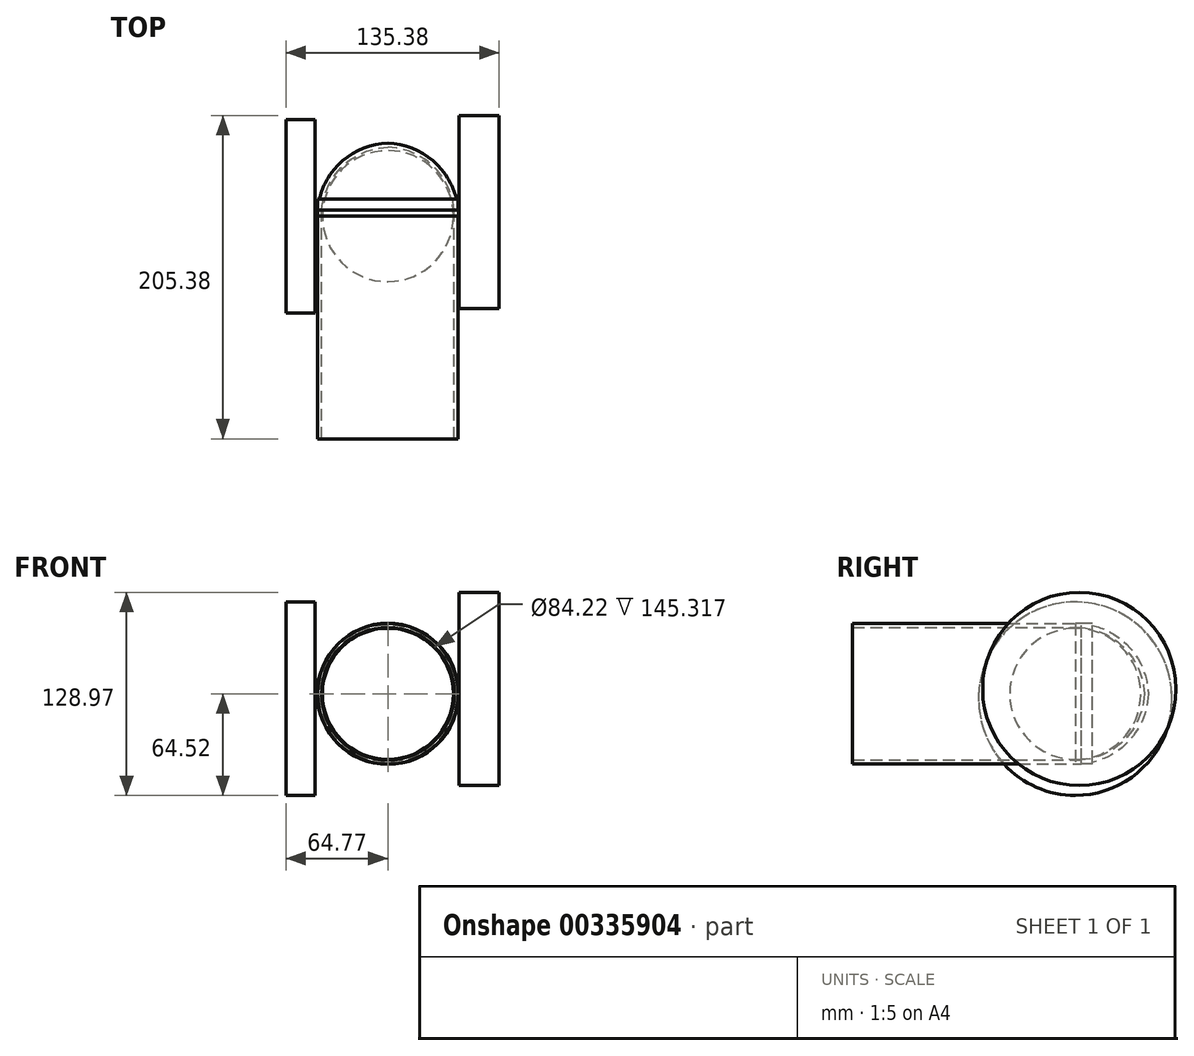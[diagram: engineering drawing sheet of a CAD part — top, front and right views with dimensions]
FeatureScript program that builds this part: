
annotation { "Feature Type Name" : "Feature", "Feature Type Description" : "" }
export const myFeature = defineFeature(function(context is Context, id is Id, definition is map)
    precondition{}
    {
        {
            var Q0;
            Q0=qCreatedBy(makeId("Front.planeOp"),FACE);
            var sketch = newSketch(context, id + "F0", { "sketchPlane" : qUnion([Q0])});
            skCircle(sketch, "E0", {"center": v(0, 0) * mm, "radius": 44.65 * mm});
            skSolve(sketch);
        }
        {
            var Q0;
            Q0 = qSketchRegion(id + "F0", true);
            extrude(context, id + "F1", {"entities" : qUnion([Q0]), "depth" : 76.2 * mm});
        }
        {
            var Q0;
            Q0=makeQuery(id+"F1.opExtrude","CAP_FACE",FACE,{"disambiguationData":[OSD([sQuery(id+"F0.wireOp",EDGE,"E0")])],"isStart":false});
            var sketch = newSketch(context, id + "F2", { "sketchPlane" : qUnion([Q0])});
            skSolve(sketch);
        }
        {
            var Q0;
            Q0=makeQuery(id+"F2.imprint","IMPRINT",FACE,{"disambiguationData":[TD([[makeQuery(id+"F2.imprint","IMPRINT",EDGE,{"derivedFrom":makeQuery(id+"F1.opExtrude","CAP_EDGE",EDGE,{"disambiguationData":[OSD([sQuery(id+"F0.wireOp",EDGE,"E0")])],"isStart":false})}),1.0]])]});
            extrude(context, id + "F3", {"entities" : qUnion([Q0]), "operationType" : NewBodyOperationType.ADD, "depth" : 25.4 * mm});
        }
        {
            var Q0;
            Q0=makeQuery(id+"F3.opExtrude","CAP_FACE",FACE,{"disambiguationData":[OSD([sQuery(id+"F0.wireOp",EDGE,"E0")])],"isStart":false});
            shell(context, id + "F4", {"entities" : qUnion([Q0]), "thickness" : 2.54 * mm});
        }
        {
            var Q0;
            Q0=qCreatedBy(makeId("Top.planeOp"),FACE);
            var sketch = newSketch(context, id + "F5", { "sketchPlane" : qUnion([Q0])});
            skArc(sketch, "E1", {"start": v(44.82, 0) * mm, "mid": v(31.78, 32.24) * mm, "end": v(0, 46.34) * mm});
            skLineSegment(sketch, "E2", {"start": v(0, 0) * mm, "end": v(44.82, 0) * mm});
            skLineSegment(sketch, "E3", {"start": v(0, 46.34) * mm, "end": v(0, 0) * mm});
            skSolve(sketch);
        }
        {
            var Q0;
            Q0=makeQuery(id+"F5.imprint","IMPRINT",FACE,{"disambiguationData":[TD([[makeQuery(id+"F5.imprint","IMPRINT",EDGE,{"derivedFrom":sQuery(id+"F5.wireOp",EDGE,"E1")}),1.0]])]});
            var Q1;
            Q1=sQuery(id+"F5.wireOp",EDGE,"E3");
            revolve(context, id + "F6", {"operationType" : NewBodyOperationType.ADD, "entities" : qUnion([Q0]), "axis" : qUnion([Q1]), "revolveType" : RevolveType.FULL});
        }
        {
            var Q0;
            {var subQ0=sQuery(id+"F0.wireOp",EDGE,"E0");Q0=makeQuery(id+"F4.opShell","OFFSET_FACE",FACE,{"disambiguationData":[OSD([subQ0]),TDD([makeQuery(id+"F1.opExtrude","CAP_FACE",FACE,{"disambiguationData":[OSD([subQ0])],"isStart":true})])]});}
            var sketch = newSketch(context, id + "F7", { "sketchPlane" : qUnion([Q0])});
            skCircle(sketch, "E4", {"center": v(0, 0) * mm, "radius": 42.16 * mm});
            skSolve(sketch);
        }
        {
            var Q0;
            Q0 = qSketchRegion(id + "F7", true);
            extrude(context, id + "F8", {"entities" : qUnion([Q0]), "operationType" : NewBodyOperationType.ADD, "depth" : 35.81 * mm});
        }
        {
            var Q0;
            Q0=qCreatedBy(makeId("Front.planeOp"),FACE);
            var sketch = newSketch(context, id + "F9", { "sketchPlane" : qUnion([Q0])});
            skCircle(sketch, "E5", {"center": v(0, 0) * mm, "radius": 41.61 * mm});
            skLineSegment(sketch, "E6", {"start": v(0, -41.61) * mm, "end": v(0, 41.61) * mm});
            skSolve(sketch);
        }
        {
            var Q0;
            {var subQ0=sQuery(id+"F9.wireOp",EDGE,"E6");Q0=makeQuery(id+"F9.imprint","IMPRINT",FACE,{"disambiguationData":[TD([[makeQuery(id+"F9.imprint","IMPRINT",EDGE,{"derivedFrom":subQ0}),-1.0]])]});}
            var Q1;
            Q1=sQuery(id+"F9.wireOp",EDGE,"E6");
            revolve(context, id + "F10", {"entities" : qUnion([Q0]), "axis" : qUnion([Q1]), "revolveType" : RevolveType.FULL});
        }
        {
            var Q0;
            Q0=makeQuery(id+"F8.opExtrude","CAP_FACE",FACE,{"disambiguationData":[OSD([sQuery(id+"F7.wireOp",EDGE,"E4")])],"isStart":false});
            shell(context, id + "F11", {"entities" : qUnion([Q0]), "thickness" : 2.54 * mm});
        }
        {
            var Q0;
            Q0=makeQuery(id+"F3.opExtrude","CAP_FACE",FACE,{"disambiguationData":[OSD([sQuery(id+"F0.wireOp",EDGE,"E0")])],"isStart":false});
            extrude(context, id + "F12", {"entities" : qUnion([Q0]), "operationType" : NewBodyOperationType.ADD, "depth" : 39.88 * mm});
        }
        {
            var Q0;
            Q0=makeQuery(id+"F12.opExtrude","CAP_FACE",FACE,{"disambiguationData":[OSD([sQuery(id+"F0.wireOp",EDGE,"E0")])],"isStart":false});
            extrude(context, id + "F13", {"entities" : qUnion([Q0]), "operationType" : NewBodyOperationType.ADD, "depth" : -152.4 * mm});
        }
        {
            var Q0;
            Q0=qCreatedBy(makeId("Right.planeOp"),FACE);
            cPlane(context, id + "F14", {"entities" : qUnion([Q0]), "cplaneType" : CPlaneType.OFFSET, "offset" : 46.23 * mm, "oppositeDirection" : true, "width" : 152.4 * mm, "height" : 152.4 * mm});
        }
        {
            var Q0;
            Q0=qCreatedBy(id+"F14.planeOp",FACE);
            var sketch = newSketch(context, id + "F15", { "sketchPlane" : qUnion([Q0])});
            skCircle(sketch, "E7", {"center": v(0, -3.08) * mm, "radius": 61.44 * mm});
            skSolve(sketch);
        }
        {
            var Q0;
            Q0=makeQuery(id+"F15.imprint","IMPRINT",FACE,{"disambiguationData":[TD([[makeQuery(id+"F15.imprint","IMPRINT",EDGE,{"derivedFrom":sQuery(id+"F15.wireOp",EDGE,"E7")}),1.0]])]});
            extrude(context, id + "F16", {"entities" : qUnion([Q0]), "oppositeDirection" : true, "depth" : 18.54 * mm});
        }
        {
            var Q0;
            Q0=qCreatedBy(makeId("Right.planeOp"),FACE);
            cPlane(context, id + "F17", {"entities" : qUnion([Q0]), "cplaneType" : CPlaneType.OFFSET, "offset" : 45.2 * mm, "width" : 152.4 * mm, "height" : 152.4 * mm});
        }
        {
            var Q0;
            Q0=qCreatedBy(id+"F17.planeOp",FACE);
            var sketch = newSketch(context, id + "F18", { "sketchPlane" : qUnion([Q0])});
            skCircle(sketch, "E8", {"center": v(2.54, 3.09) * mm, "radius": 61.36 * mm});
            skSolve(sketch);
        }
        {
            var Q0;
            Q0=makeQuery(id+"F18.imprint","IMPRINT",FACE,{"disambiguationData":[TD([[makeQuery(id+"F18.imprint","IMPRINT",EDGE,{"derivedFrom":sQuery(id+"F18.wireOp",EDGE,"E8")}),1.0]])]});
            extrude(context, id + "F19", {"entities" : qUnion([Q0]), "depth" : 25.4 * mm});
        }
        {
            var Q0;
            Q0=makeQuery(id+"F15.imprint","IMPRINT",BODY,{"disambiguationData":[TD([[makeQuery(id+"F15.imprint","IMPRINT",FACE,{"disambiguationData":[TD([[makeQuery(id+"F15.imprint","IMPRINT",EDGE,{"derivedFrom":sQuery(id+"F15.wireOp",EDGE,"E7")}),1.0]])]}),1.0]])]});
            var Q1;
            Q1=qCreatedBy(makeId("Right.planeOp"),FACE);
            mirror(context, id + "F20", {"entities" : qUnion([Q0]), "mirrorPlane" : qUnion([Q1])});
        }
    });
